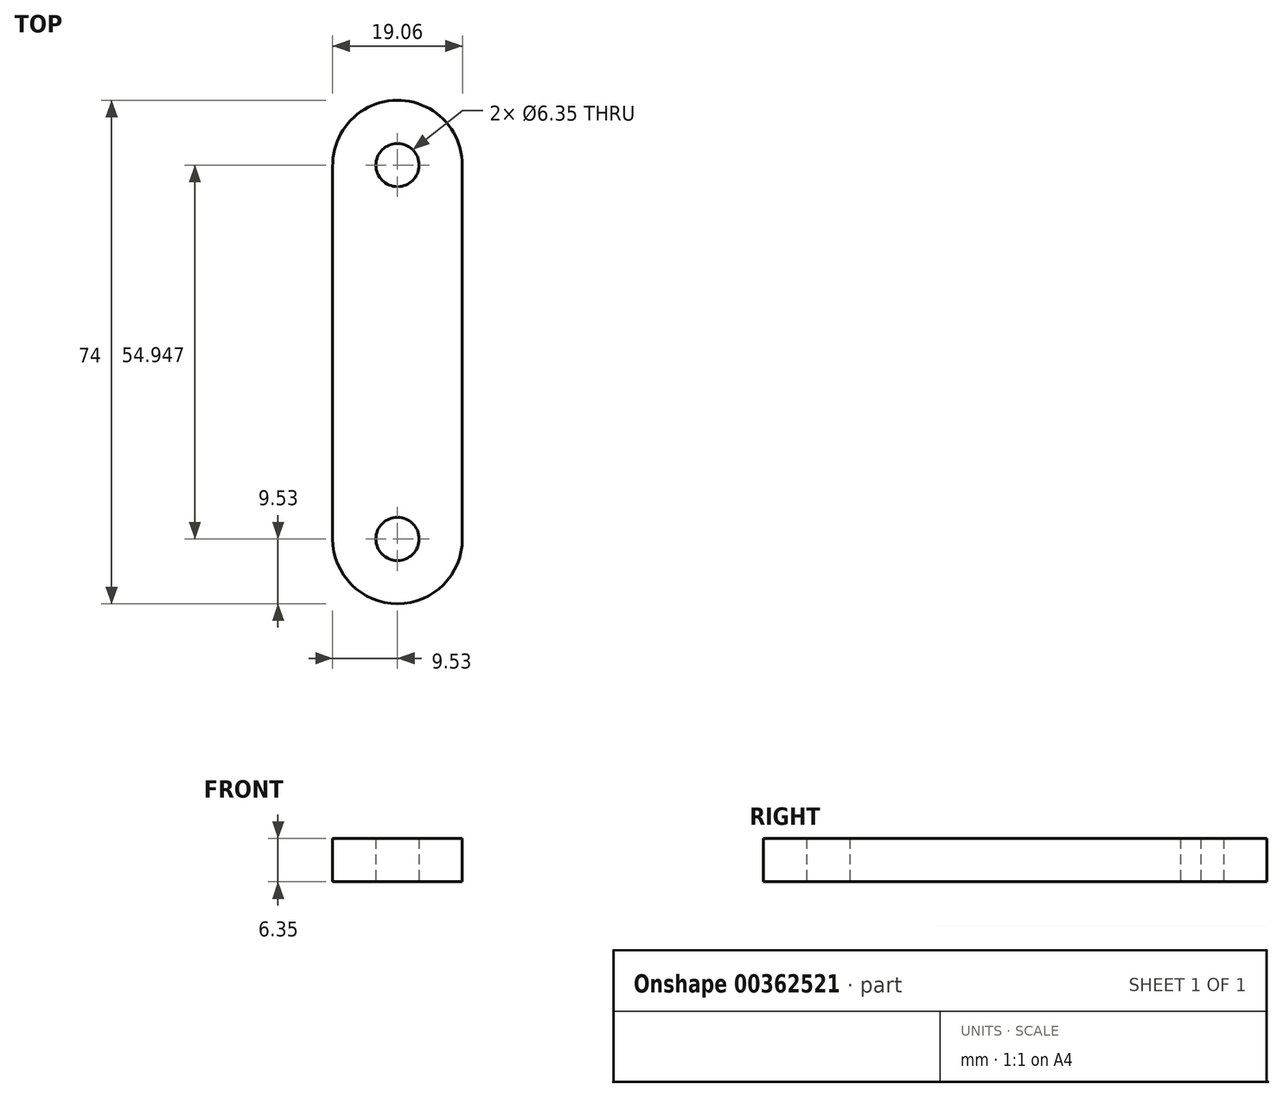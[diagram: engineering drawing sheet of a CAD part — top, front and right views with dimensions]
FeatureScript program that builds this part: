
annotation { "Feature Type Name" : "Feature", "Feature Type Description" : "" }
export const myFeature = defineFeature(function(context is Context, id is Id, definition is map)
    precondition{}
    {
        {
            var Q0;
            Q0=qCreatedBy(makeId("Top.planeOp"),FACE);
            var sketch = newSketch(context, id + "F0", { "sketchPlane" : qUnion([Q0])});
            skLineSegment(sketch, "E0", {"start": v(0, 0) * mm, "end": v(0, 54.95) * mm});
            skCircle(sketch, "E1", {"center": v(0, 54.95) * mm, "radius": 3.18 * mm});
            skCircle(sketch, "E2", {"center": v(0, 0) * mm, "radius": 3.18 * mm});
            skCircle(sketch, "E3", {"center": v(0, 54.95) * mm, "radius": 9.53 * mm});
            skCircle(sketch, "E4", {"center": v(0, 0) * mm, "radius": 9.53 * mm});
            skLineSegment(sketch, "E5", {"start": v(-9.52, 54.74) * mm, "end": v(-9.53, 0) * mm});
            skLineSegment(sketch, "E6", {"start": v(-9.53, 0) * mm, "end": v(9.53, 0) * mm});
            skLineSegment(sketch, "E7", {"start": v(9.53, 0) * mm, "end": v(9.53, 54.95) * mm});
            skSolve(sketch);
        }
        {
            var Q0;
            Q0 = qSketchRegion(id + "F0", true);
            extrude(context, id + "F1", {"entities" : qUnion([Q0]), "depth" : 6.35 * mm});
        }
    });
